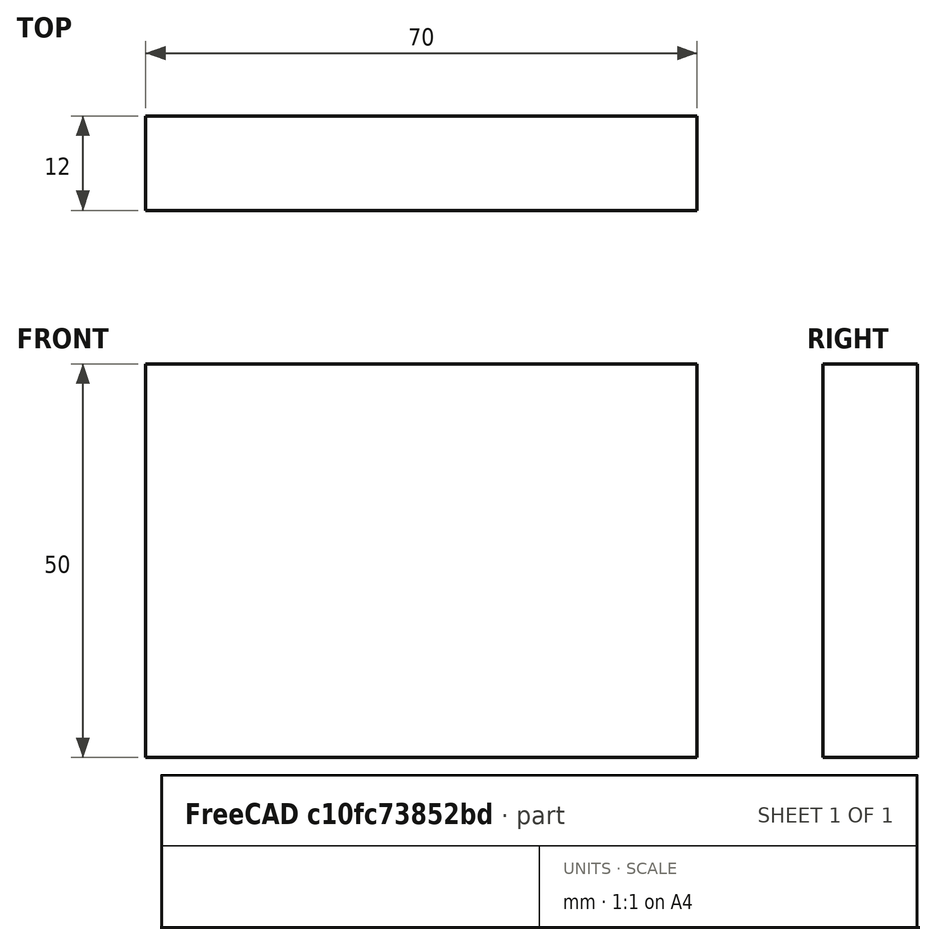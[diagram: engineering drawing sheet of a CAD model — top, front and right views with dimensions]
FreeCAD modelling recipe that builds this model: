
FCSTD DOCUMENT  (FreeCAD 0.15R4671 (Git))
Label: Flat Bar 70x12 EN10058 S235JR
License: All rights reserved
LicenseURL: http://en.wikipedia.org/wiki/All_rights_reserved
objects: Sketcher::SketchObject×1, Part::Extrusion×1
note: 2 computed .brp shape members not serialized (recipe doc carries the construction recipe); baked Part::Feature solids carry a one-line shape summary decoded from their .brp

FEATURE [Sketcher::SketchObject] Sketch
  sketch-geometry (4):
    g0: LineSegment StartX=-35 StartY=-6 StartZ=0 EndX=35 EndY=-6 EndZ=0
    g1: LineSegment StartX=35 StartY=-6 StartZ=0 EndX=35 EndY=6 EndZ=0
    g2: LineSegment StartX=35 StartY=6 StartZ=0 EndX=-35 EndY=6 EndZ=0
    g3: LineSegment StartX=-35 StartY=6 StartZ=0 EndX=-35 EndY=-6 EndZ=0
  constraints (12):
    c: Coincident(g0,g1)
    c: Coincident(g1,g2)
    c: Coincident(g2,g3)
    c: Coincident(g3,g0)
    c: Horizontal(g0)
    c: Horizontal(g2)
    c: Vertical(g1)
    c: Vertical(g3)
    c: Symmetric(g1,g2,g-2)
    c: Symmetric(g0,g1,g-1)
    c: DistanceY(g1) = 12
    c: DistanceX(g0) = 70
FEATURE [Part::Extrusion] Extrude  label="Flat Bar 70x12 EN10058 S235JR"
  Base = -> Sketch
  Dir = (0,0,50)
  Solid = true
